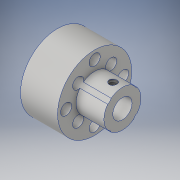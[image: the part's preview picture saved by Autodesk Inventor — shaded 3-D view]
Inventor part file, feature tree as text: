
AUTODESK INVENTOR PART (.ipt)
format: ipt  version: 2017 (Build 210142000, 142)  size: 167,424 bytes
history: native  units: in
note: dims shown in document units (in); Inventor stores cm internally (conversion verified against a paired STEP export)
features: sketch x3, hole x3, extrude x2, plane x1, projected_geometry x1
ambient origin geometry x8: Origin, YZ Plane, XZ Plane, XY Plane, X Axis, Y Axis, Z Axis, Center Point
bodies: Solid1 (feature_tree)
feature tree (10):
  sketch  "Sketch1"  dims[d0=1.0in d6=45.0deg]
  extrude  "Extrusion1"  TaperAngle=45.0deg  [1 undecoded]
  extrude  "Extrusion2"  Depth=0.5in TaperAngle=0.0deg
  hole  "Hole1"  [1 undecoded]
  hole  "Hole2"  [1 undecoded]
  plane  "Work Plane2"
  hole  "Hole3"  [1 undecoded]
  sketch  "Sketch2"  dims[d15=0.26in d16=0.5in d17=0.0in]
  sketch  "Sketch5"  dims[d18=0.5in d19=0.375in d20=0.0in d21=1.5748in d23=360.0deg d25=0.385in d26=1.5748in d28=360.0deg d30=0.15in d31=0.75in d32=0.375in d33=0.25in d34=0.5635in d35=1.0in d36=0.8108in d37=0.15in d38=0.75in d39=0.375in d40=0.25in d41=0.5635in d42=1.0in d43=0.8108in d46=0.125in d47=0.104in d48=0.276in d49=0.375in d50=0.25in d51=0.5635in d52=0.432in d53=0.8108in]
  projected_geometry  "Projected Loop1"
note: 4 required parameter values undecoded (feature->parameter linkage not recoverable at this tier; creation-order binding heuristic only, values carry confidence <= 0.55)
